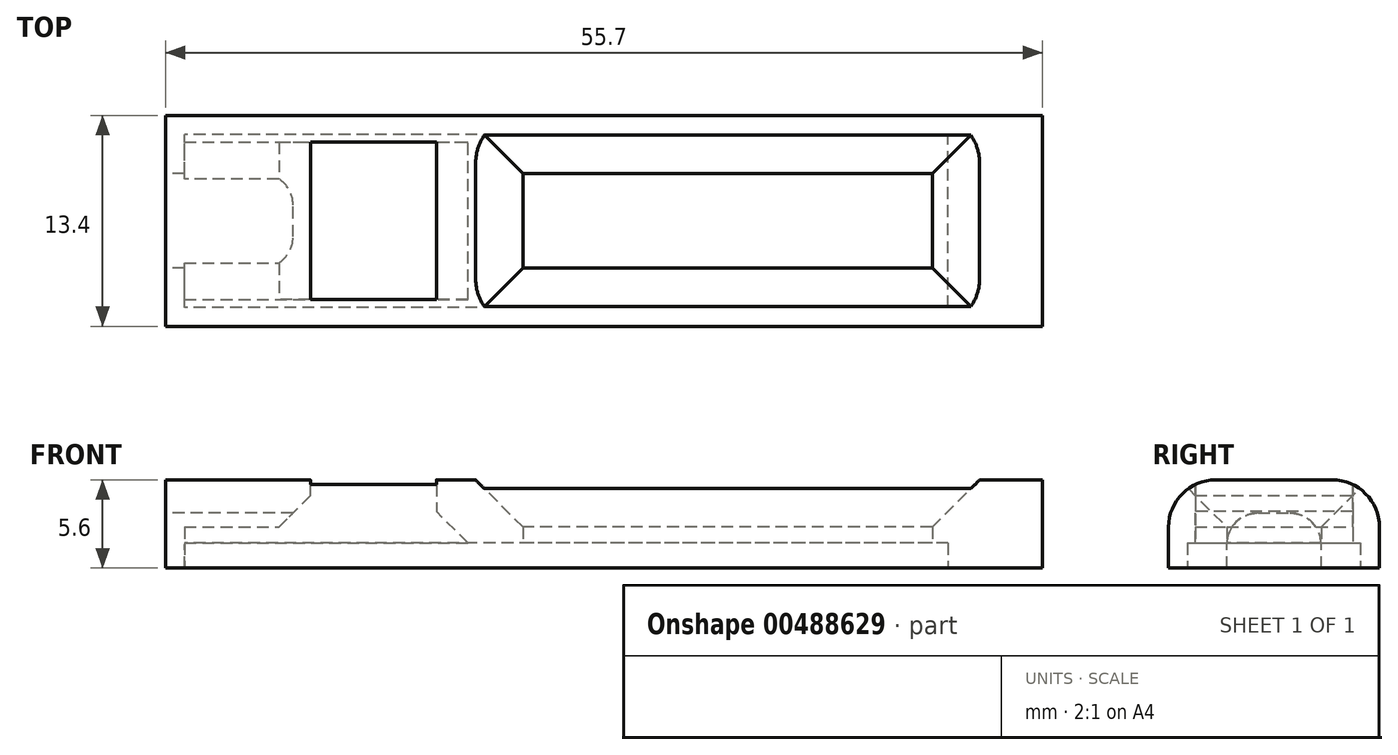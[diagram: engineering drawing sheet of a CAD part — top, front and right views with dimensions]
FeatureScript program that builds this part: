
annotation { "Feature Type Name" : "Feature", "Feature Type Description" : "" }
export const myFeature = defineFeature(function(context is Context, id is Id, definition is map)
    precondition{}
    {
        {
            var Q0;
            Q0=qCreatedBy(makeId("Top.planeOp"),FACE);
            var sketch = newSketch(context, id + "F0", { "sketchPlane" : qUnion([Q0])});
            skLineSegment(sketch, "E0.bottom", {"start": v(0, 0) * mm, "end": v(-47.5, 0) * mm});
            skLineSegment(sketch, "E0.top", {"start": v(0, 11) * mm, "end": v(-47.5, 11) * mm});
            skLineSegment(sketch, "E0.left", {"start": v(0, 0) * mm, "end": v(0, 11) * mm});
            skLineSegment(sketch, "E0.right", {"start": v(-47.5, 0) * mm, "end": v(-47.5, 11) * mm});
            skLineSegment(sketch, "E1.bottom", {"start": v(7, 12.2) * mm, "end": v(-48.7, 12.2) * mm});
            skLineSegment(sketch, "E1.top", {"start": v(7, -1.2) * mm, "end": v(-48.7, -1.2) * mm});
            skLineSegment(sketch, "E1.left", {"start": v(7, 12.2) * mm, "end": v(7, -1.2) * mm});
            skLineSegment(sketch, "E1.right", {"start": v(-48.7, 12.2) * mm, "end": v(-48.7, -1.2) * mm});
            skLineSegment(sketch, "E2", {"start": v(-47.5, 5.5) * mm, "end": v(-48.7, 5.5) * mm, "construction": true});
            skLineSegment(sketch, "E3", {"start": v(-23.75, 11) * mm, "end": v(-23.75, 12.2) * mm, "construction": true});
            skLineSegment(sketch, "E4", {"start": v(-23.75, 0) * mm, "end": v(-23.75, -1.2) * mm, "construction": true});
            skLineSegment(sketch, "E5", {"start": v(0, 5.5) * mm, "end": v(7, 5.5) * mm, "construction": true});
            skLineSegment(sketch, "E6.bottom", {"start": v(0, 0) * mm, "end": v(1, 0) * mm});
            skLineSegment(sketch, "E6.top", {"start": v(0, 11) * mm, "end": v(1, 11) * mm});
            skLineSegment(sketch, "E6.right", {"start": v(1, 0) * mm, "end": v(1, 11) * mm});
            skSolve(sketch);
        }
        {
            var Q0;
            Q0 = qSketchRegion(id + "F0", true);
            extrude(context, id + "F1", {"entities" : qUnion([Q0]), "depth" : 1.6 * mm, "offsetDistance" : 25 * mm});
        }
        {
            var Q0;
            Q0=makeQuery(id+"F1.opExtrude","CAP_FACE",FACE,{"disambiguationData":[OSD([sQuery(id+"F0.wireOp",EDGE,"E0.bottom"),sQuery(id+"F0.wireOp",EDGE,"E0.top"),sQuery(id+"F0.wireOp",EDGE,"E0.left"),sQuery(id+"F0.wireOp",EDGE,"E0.right"),sQuery(id+"F0.wireOp",EDGE,"E1.bottom"),sQuery(id+"F0.wireOp",EDGE,"E1.top"),sQuery(id+"F0.wireOp",EDGE,"E1.left"),sQuery(id+"F0.wireOp",EDGE,"E1.right")])],"isStart":false});
            var sketch = newSketch(context, id + "F2", { "sketchPlane" : qUnion([Q0])});
            skLineSegment(sketch, "E7.bottom", {"start": v(7, -1.2) * mm, "end": v(-48.7, -1.2) * mm});
            skLineSegment(sketch, "E7.top", {"start": v(7, 12.2) * mm, "end": v(-48.7, 12.2) * mm});
            skLineSegment(sketch, "E7.left", {"start": v(7, -1.2) * mm, "end": v(7, 12.2) * mm});
            skLineSegment(sketch, "E7.right", {"start": v(-48.7, -1.2) * mm, "end": v(-48.7, 12.2) * mm});
            skLineSegment(sketch, "E8.bottom", {"start": v(0, 8.5) * mm, "end": v(-26, 8.5) * mm});
            skLineSegment(sketch, "E8.top", {"start": v(0, 2.5) * mm, "end": v(-26, 2.5) * mm});
            skLineSegment(sketch, "E8.left", {"start": v(0, 8.5) * mm, "end": v(0, 2.5) * mm});
            skLineSegment(sketch, "E8.right", {"start": v(-26, 8.5) * mm, "end": v(-26, 2.5) * mm});
            skLineSegment(sketch, "E9", {"start": v(-5.07, 11) * mm, "end": v(-5.07, 8.5) * mm, "construction": true});
            skLineSegment(sketch, "E10", {"start": v(-5.48, 2.5) * mm, "end": v(-5.48, 0) * mm, "construction": true});
            skLineSegment(sketch, "E11.bottom", {"start": v(-47.5, 10.5) * mm, "end": v(-31.5, 10.5) * mm});
            skLineSegment(sketch, "E11.top", {"start": v(-47.5, 0.5) * mm, "end": v(-31.5, 0.5) * mm});
            skLineSegment(sketch, "E11.left", {"start": v(-47.5, 10.5) * mm, "end": v(-47.5, 0.5) * mm});
            skLineSegment(sketch, "E11.right", {"start": v(-31.5, 10.5) * mm, "end": v(-31.5, 0.5) * mm});
            skLineSegment(sketch, "E12", {"start": v(-43.85, 11) * mm, "end": v(-43.85, 10.5) * mm, "construction": true});
            skPoint(sketch, "E12.endSnap0", {"position": v(-39.5, 10.5) * mm});
            skLineSegment(sketch, "E13", {"start": v(-44.06, 0.5) * mm, "end": v(-44.06, 0) * mm, "construction": true});
            skLineSegment(sketch, "E14.left", {"start": v(0, 2.5) * mm, "end": v(0, 8.5) * mm});
            skSolve(sketch);
        }
        {
            var Q0;
            {var subQ6=sQuery(id+"F2.wireOp",EDGE,"E8.bottom");Q0=makeQuery(id+"F2.imprint","IMPRINT",FACE,{"disambiguationData":[TD([[makeQuery(id+"F2.imprint","IMPRINT",EDGE,{"derivedFrom":subQ6}),-1.0]])]});}
            var Q1;
            Q1=makeQuery(id+"F2.imprint","IMPRINT",FACE,{"disambiguationData":[TD([[makeQuery(id+"F2.imprint","IMPRINT",EDGE,{"derivedFrom":sQuery(id+"F2.wireOp",EDGE,"E7.bottom")}),-1.0]])]});
            extrude(context, id + "F3", {"entities" : qUnion([Q0, Q1]), "operationType" : NewBodyOperationType.ADD, "depth" : 4 * mm});
        }
        {
            var Q0;
            Q0=makeQuery(id+"F3.opExtrude","CAP_FACE",FACE,{"disambiguationData":[OSD([sQuery(id+"F2.wireOp",EDGE,"E7.bottom"),sQuery(id+"F2.wireOp",EDGE,"E7.top"),sQuery(id+"F2.wireOp",EDGE,"E7.left"),sQuery(id+"F2.wireOp",EDGE,"E7.right"),sQuery(id+"F2.wireOp",EDGE,"E8.bottom"),sQuery(id+"F2.wireOp",EDGE,"E8.top"),sQuery(id+"F2.wireOp",EDGE,"E8.left"),sQuery(id+"F2.wireOp",EDGE,"E8.right"),sQuery(id+"F2.wireOp",EDGE,"E11.bottom"),sQuery(id+"F2.wireOp",EDGE,"E11.top"),sQuery(id+"F2.wireOp",EDGE,"E11.left"),sQuery(id+"F2.wireOp",EDGE,"E11.right")])],"isStart":false});
            var sketch = newSketch(context, id + "F4", { "sketchPlane" : qUnion([Q0])});
            skLineSegment(sketch, "E15.bottom", {"start": v(-48.7, 12.2) * mm, "end": v(-39.5, 12.2) * mm});
            skLineSegment(sketch, "E15.top", {"start": v(-48.7, -1.2) * mm, "end": v(-39.5, -1.2) * mm});
            skLineSegment(sketch, "E15.left", {"start": v(-48.7, 12.2) * mm, "end": v(-48.7, -1.2) * mm});
            skLineSegment(sketch, "E15.right", {"start": v(-39.5, 12.2) * mm, "end": v(-39.5, -1.2) * mm});
            skLineSegment(sketch, "E16", {"start": v(-39.5, 5.5) * mm, "end": v(-31.5, 5.5) * mm, "construction": true});
            skSolve(sketch);
        }
        {
            var Q0;
            {var subQ5=makeQuery(id+"F3.opExtrude","CAP_EDGE",EDGE,{"disambiguationData":[OSD([sQuery(id+"F2.wireOp",EDGE,"E11.left")])],"isStart":false});Q0=makeQuery(id+"F4.imprint","IMPRINT",FACE,{"disambiguationData":[TD([[makeQuery(id+"F4.imprint","IMPRINT",EDGE,{"derivedFrom":subQ5}),-1.0]])]});}
            var Q1;
            {var subQ1=sQuery(id+"F4.wireOp",EDGE,"E15.bottom");Q1=makeQuery(id+"F4.imprint","IMPRINT",FACE,{"disambiguationData":[TD([[makeQuery(id+"F4.imprint","IMPRINT",EDGE,{"derivedFrom":subQ1}),1.0]])]});}
            extrude(context, id + "F5", {"entities" : qUnion([Q0, Q1]), "operationType" : NewBodyOperationType.ADD, "oppositeDirection" : true, "depth" : 3 * mm});
        }
        {
            var Q0;
            Q0=makeQuery(id+"F3.opExtrude","CAP_EDGE",EDGE,{"disambiguationData":[OSD([sQuery(id+"F2.wireOp",EDGE,"E7.top")])],"isStart":false});
            var Q1;
            Q1=makeQuery(id+"F3.opExtrude","CAP_EDGE",EDGE,{"disambiguationData":[OSD([sQuery(id+"F2.wireOp",EDGE,"E7.bottom")])],"isStart":false});
            fillet(context, id + "F6", {"entities" : qUnion([Q0, Q1]), "radius" : 3 * mm, "tangentPropagation" : true, "allowEdgeOverflow" : false});
        }
        {
            var Q0;
            Q0=makeQuery(id+"F3.boolean.opBoolean","MERGE",FACE,{"derivedFrom":[makeQuery(id+"F1.opExtrude","SWEPT_FACE",FACE,{"disambiguationData":[OSD([sQuery(id+"F0.wireOp",EDGE,"E1.right")])]}),makeQuery(id+"F3.opExtrude","SWEPT_FACE",FACE,{"disambiguationData":[OSD([sQuery(id+"F2.wireOp",EDGE,"E7.right")])]})]});
            var sketch = newSketch(context, id + "F7", { "sketchPlane" : qUnion([Q0])});
            skLineSegment(sketch, "E17.bottom", {"start": v(-2.5, 0) * mm, "end": v(-8.5, 0) * mm});
            skLineSegment(sketch, "E17.top", {"start": v(-2.5, 3.5) * mm, "end": v(-8.5, 3.5) * mm});
            skLineSegment(sketch, "E17.left", {"start": v(-2.5, 0) * mm, "end": v(-2.5, 3.5) * mm});
            skLineSegment(sketch, "E17.right", {"start": v(-8.5, 0) * mm, "end": v(-8.5, 3.5) * mm});
            skLineSegment(sketch, "E18", {"start": v(-8.5, 1.75) * mm, "end": v(-12.2, 1.75) * mm, "construction": true});
            skLineSegment(sketch, "E19", {"start": v(-2.5, 1.75) * mm, "end": v(1.2, 1.75) * mm, "construction": true});
            skSolve(sketch);
        }
        {
            var Q0;
            Q0=makeQuery(id+"F7.imprint","IMPRINT",FACE,{"disambiguationData":[TD([[makeQuery(id+"F7.imprint","IMPRINT",EDGE,{"derivedFrom":sQuery(id+"F7.wireOp",EDGE,"E17.bottom")}),1.0]])]});
            extrude(context, id + "F8", {"entities" : qUnion([Q0]), "operationType" : NewBodyOperationType.REMOVE, "oppositeDirection" : true, "depth" : 10 * mm});
        }
        {
            var Q0;
            Q0=makeQuery(id+"F8.boolean.opBoolean","COPY",EDGE,{"derivedFrom":makeQuery(id+"F8.opExtrude","SWEPT_EDGE",EDGE,{"disambiguationData":[OSD([sQuery(id+"F7.wireOp",EDGE,"E17.top"),sQuery(id+"F7.wireOp",EDGE,"E17.right")])]})});
            var Q1;
            Q1=makeQuery(id+"F8.boolean.opBoolean","COPY",EDGE,{"derivedFrom":makeQuery(id+"F8.opExtrude","SWEPT_EDGE",EDGE,{"disambiguationData":[OSD([sQuery(id+"F7.wireOp",EDGE,"E17.top"),sQuery(id+"F7.wireOp",EDGE,"E17.left")])]})});
            fillet(context, id + "F9", {"entities" : qUnion([Q0, Q1]), "radius" : 2 * mm, "tangentPropagation" : true, "allowEdgeOverflow" : false});
        }
        {
            var Q0;
            Q0=makeQuery(id+"F3.opExtrude","CAP_EDGE",EDGE,{"disambiguationData":[OSD([sQuery(id+"F2.wireOp",EDGE,"E8.right")])],"isStart":false});
            var Q1;
            Q1=makeQuery(id+"F3.opExtrude","CAP_EDGE",EDGE,{"disambiguationData":[OSD([sQuery(id+"F2.wireOp",EDGE,"E8.bottom")])],"isStart":false});
            var Q2;
            Q2=makeQuery(id+"F3.opExtrude","CAP_EDGE",EDGE,{"disambiguationData":[OSD([sQuery(id+"F2.wireOp",EDGE,"E8.top")])],"isStart":false});
            var Q3;
            Q3=makeQuery(id+"F3.opExtrude","CAP_EDGE",EDGE,{"disambiguationData":[OSD([sQuery(id+"F2.wireOp",EDGE,"E8.left")])],"isStart":false});
            var Q4;
            Q4=makeQuery(id+"F3.opExtrude","CAP_EDGE",EDGE,{"disambiguationData":[OSD([sQuery(id+"F2.wireOp",EDGE,"E14.left")])],"isStart":false});
            chamfer(context, id + "F10", {"entities" : qUnion([Q0, Q1, Q2, Q3, Q4]), "width" : 3 * mm, "tangentPropagation" : true});
        }
        {
            var Q0;
            Q0=makeQuery(id+"F5.opExtrude","CAP_EDGE",EDGE,{"disambiguationData":[OSD([sQuery(id+"F4.wireOp",EDGE,"E15.right")])],"isStart":false});
            var Q1;
            Q1=makeQuery(id+"F3.opExtrude","CAP_EDGE",EDGE,{"disambiguationData":[OSD([sQuery(id+"F2.wireOp",EDGE,"E11.right")])],"isStart":true});
            chamfer(context, id + "F11", {"entities" : qUnion([Q0, Q1]), "width" : 2 * mm, "tangentPropagation" : true});
        }
    });
